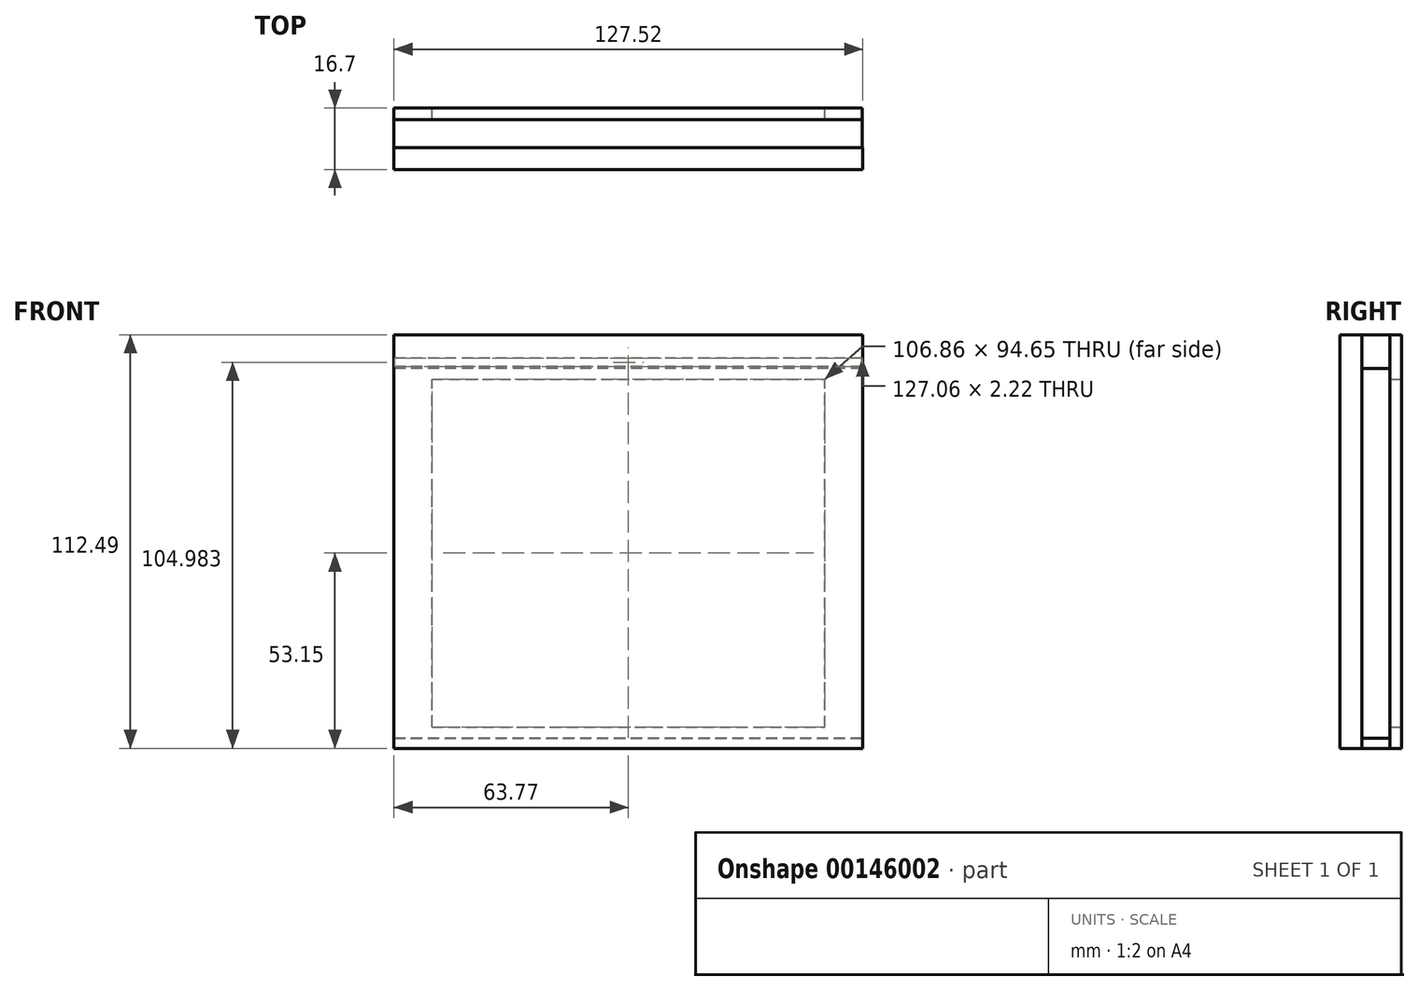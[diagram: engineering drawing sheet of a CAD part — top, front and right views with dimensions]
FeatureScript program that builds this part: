
annotation { "Feature Type Name" : "Feature", "Feature Type Description" : "" }
export const myFeature = defineFeature(function(context is Context, id is Id, definition is map)
    precondition{}
    {
        {
            var Q0;
            Q0=qCreatedBy(makeId("Front.planeOp"),FACE);
            var sketch = newSketch(context, id + "F0", { "sketchPlane" : qUnion([Q0])});
            skLineSegment(sketch, "E0.bottom", {"start": v(63.53, -52.94) * mm, "end": v(-63.53, -52.94) * mm});
            skLineSegment(sketch, "E0.top", {"start": v(63.53, 52.94) * mm, "end": v(-63.53, 52.94) * mm});
            skLineSegment(sketch, "E0.left", {"start": v(63.53, -52.94) * mm, "end": v(63.53, 52.94) * mm});
            skLineSegment(sketch, "E0.right", {"start": v(-63.53, -52.94) * mm, "end": v(-63.53, 52.94) * mm});
            skPoint(sketch, "E0.middle", {"position": v(0, 0) * mm});
            skSolve(sketch);
        }
        {
            var Q0;
            Q0=qSketchRegion(id+"F0",true);
            extrude(context, id + "F1", {"entities" : qUnion([Q0]), "depth" : 10.16 * mm});
        }
        {
            var Q0;
            Q0=qCreatedBy(makeId("Front.planeOp"),FACE);
            var sketch = newSketch(context, id + "F2", { "sketchPlane" : qUnion([Q0])});
            skLineSegment(sketch, "E1.bottom", {"start": v(-54.5, 52.94) * mm, "end": v(54.5, 52.94) * mm});
            skLineSegment(sketch, "E1.top", {"start": v(-54.5, -52.94) * mm, "end": v(54.5, -52.94) * mm});
            skLineSegment(sketch, "E1.left", {"start": v(-54.5, 52.94) * mm, "end": v(-54.5, -52.94) * mm});
            skLineSegment(sketch, "E1.right", {"start": v(54.5, 52.94) * mm, "end": v(54.5, -52.94) * mm});
            skPoint(sketch, "E1.middle", {"position": v(0, 0) * mm});
            skSolve(sketch);
        }
        {
            var Q0;
            Q0=makeQuery(id+"F2.imprint","IMPRINT",FACE,{"disambiguationData":[TD([[makeQuery(id+"F2.imprint","IMPRINT",EDGE,{"derivedFrom":sQuery(id+"F2.wireOp",EDGE,"E1.bottom")}),-1.0]])]});
            extrude(context, id + "F3", {"entities" : qUnion([Q0]), "operationType" : NewBodyOperationType.REMOVE, "depth" : 3.8 * mm});
        }
        {
            var Q0;
            Q0=qCreatedBy(makeId("Top.planeOp"),FACE);
            var sketch = newSketch(context, id + "F4", { "sketchPlane" : qUnion([Q0])});
            skCircle(sketch, "E2", {"center": v(-59.48, -1.57) * mm, "radius": 2.91 * mm});
            skSolve(sketch);
        }
        {
            var Q0;
            Q0=qSketchRegion(id+"F4",true);
            extrude(context, id + "F5", {"entities" : qUnion([Q0]), "operationType" : NewBodyOperationType.REMOVE, "depth" : 62.1 * mm, "hasSecondDirection" : true, "secondDirectionOppositeDirection" : true, "secondDirectionDepth" : 60.44 * mm});
        }
        {
            var Q0;
            Q0=qCreatedBy(makeId("Right.planeOp"),FACE);
            var sketch = newSketch(context, id + "F6", { "sketchPlane" : qUnion([Q0])});
            skLineSegment(sketch, "E3.bottom", {"start": v(-7.77, 50.72) * mm, "end": v(-2.1, 50.72) * mm});
            skLineSegment(sketch, "E3.top", {"start": v(-7.77, -51.05) * mm, "end": v(-2.1, -51.05) * mm});
            skLineSegment(sketch, "E3.left", {"start": v(-7.77, 50.72) * mm, "end": v(-7.77, -51.05) * mm});
            skLineSegment(sketch, "E3.right", {"start": v(-2.1, 50.72) * mm, "end": v(-2.1, -51.05) * mm});
            skSolve(sketch);
        }
        {
            var Q0;
            Q0=qSketchRegion(id+"F6",true);
            extrude(context, id + "F7", {"entities" : qUnion([Q0]), "operationType" : NewBodyOperationType.REMOVE, "oppositeDirection" : true, "depth" : 87.7 * mm, "hasSecondDirection" : true, "secondDirectionOppositeDirection" : false, "secondDirectionDepth" : 90.01 * mm});
        }
        {
            var Q0;
            Q0=qCreatedBy(makeId("Right.planeOp"),FACE);
            var sketch = newSketch(context, id + "F8", { "sketchPlane" : qUnion([Q0])});
            skLineSegment(sketch, "E4.bottom", {"start": v(-3.31, 51.47) * mm, "end": v(-4.6, 51.47) * mm});
            skLineSegment(sketch, "E4.top", {"start": v(-3.31, -50.55) * mm, "end": v(-4.6, -50.55) * mm});
            skLineSegment(sketch, "E4.left", {"start": v(-3.31, 51.47) * mm, "end": v(-3.31, -50.55) * mm});
            skLineSegment(sketch, "E4.right", {"start": v(-4.6, 51.47) * mm, "end": v(-4.6, -50.55) * mm});
            skSolve(sketch);
        }
        {
            var Q0;
            Q0=qSketchRegion(id+"F8",true);
            extrude(context, id + "F9", {"entities" : qUnion([Q0]), "operationType" : NewBodyOperationType.REMOVE, "depth" : 76.04 * mm, "hasSecondDirection" : true, "secondDirectionOppositeDirection" : true, "secondDirectionDepth" : 72.7 * mm});
        }
        {
            var Q0;
            Q0=qCreatedBy(makeId("Front.planeOp"),FACE);
            var sketch = newSketch(context, id + "F10", { "sketchPlane" : qUnion([Q0])});
            skLineSegment(sketch, "E5.bottom", {"start": v(63.53, 52.94) * mm, "end": v(-63.75, 52.94) * mm});
            skLineSegment(sketch, "E5.top", {"start": v(63.53, -53.15) * mm, "end": v(-63.75, -53.15) * mm});
            skLineSegment(sketch, "E5.left", {"start": v(63.53, 52.94) * mm, "end": v(63.53, -53.15) * mm});
            skLineSegment(sketch, "E5.right", {"start": v(-63.75, 52.94) * mm, "end": v(-63.75, -53.15) * mm});
            skSolve(sketch);
        }
        {
            var Q0;
            Q0=qSketchRegion(id+"F10",true);
            extrude(context, id + "F11", {"entities" : qUnion([Q0]), "operationType" : NewBodyOperationType.ADD, "oppositeDirection" : true, "depth" : 3.17 * mm});
        }
        {
            var Q0;
            Q0=qCreatedBy(makeId("Front.planeOp"),FACE);
            var sketch = newSketch(context, id + "F12", { "sketchPlane" : qUnion([Q0])});
            skLineSegment(sketch, "E6.bottom", {"start": v(-63.76, 52.95) * mm, "end": v(63.75, 52.95) * mm});
            skLineSegment(sketch, "E6.top", {"start": v(-63.76, -53.15) * mm, "end": v(63.75, -53.15) * mm});
            skLineSegment(sketch, "E6.left", {"start": v(-63.76, 52.95) * mm, "end": v(-63.76, -53.15) * mm});
            skLineSegment(sketch, "E6.right", {"start": v(63.75, 52.95) * mm, "end": v(63.75, -53.15) * mm});
            skSolve(sketch);
        }
        {
            var Q0;
            Q0=qSketchRegion(id+"F12",true);
            extrude(context, id + "F13", {"entities" : qUnion([Q0]), "operationType" : NewBodyOperationType.ADD, "depth" : 13.53 * mm, "hasSecondDirection" : true, "secondDirectionOppositeDirection" : false, "secondDirectionDepth" : 7.62 * mm});
        }
        {
            var Q0;
            Q0=qCreatedBy(makeId("Right.planeOp"),FACE);
            var sketch = newSketch(context, id + "F14", { "sketchPlane" : qUnion([Q0])});
            skLineSegment(sketch, "E7.bottom", {"start": v(0, 51.68) * mm, "end": v(-7.6, 51.68) * mm});
            skLineSegment(sketch, "E7.top", {"start": v(0, -51.05) * mm, "end": v(-7.6, -51.05) * mm});
            skLineSegment(sketch, "E7.left", {"start": v(0, 51.68) * mm, "end": v(0, -51.05) * mm});
            skLineSegment(sketch, "E7.right", {"start": v(-7.6, 51.68) * mm, "end": v(-7.6, -51.05) * mm});
            skSolve(sketch);
        }
        {
            var Q0;
            Q0=qSketchRegion(id+"F14",true);
            extrude(context, id + "F15", {"entities" : qUnion([Q0]), "operationType" : NewBodyOperationType.REMOVE, "depth" : 76.4 * mm, "hasSecondDirection" : true, "secondDirectionOppositeDirection" : true, "secondDirectionDepth" : 73.64 * mm});
        }
        {
            var Q0;
            Q0=qCreatedBy(makeId("Right.planeOp"),FACE);
            var sketch = newSketch(context, id + "F16", { "sketchPlane" : qUnion([Q0])});
            skLineSegment(sketch, "E8.bottom", {"start": v(-7.6, 52.99) * mm, "end": v(0, 52.99) * mm});
            skLineSegment(sketch, "E8.top", {"start": v(-7.6, 50.24) * mm, "end": v(0, 50.24) * mm});
            skLineSegment(sketch, "E8.left", {"start": v(-7.6, 52.99) * mm, "end": v(-7.6, 50.24) * mm});
            skLineSegment(sketch, "E8.right", {"start": v(0, 52.99) * mm, "end": v(0, 50.24) * mm});
            skLineSegment(sketch, "E9.bottom", {"start": v(-7.61, -53.13) * mm, "end": v(0, -53.13) * mm});
            skLineSegment(sketch, "E9.top", {"start": v(-7.61, -50.42) * mm, "end": v(0, -50.42) * mm});
            skLineSegment(sketch, "E9.left", {"start": v(-7.61, -53.13) * mm, "end": v(-7.61, -50.42) * mm});
            skLineSegment(sketch, "E9.right", {"start": v(0, -53.13) * mm, "end": v(0, -50.42) * mm});
            skSolve(sketch);
        }
        {
            var Q0;
            Q0=qSketchRegion(id+"F16",true);
            extrude(context, id + "F17", {"entities" : qUnion([Q0]), "operationType" : NewBodyOperationType.ADD, "depth" : 63.54 * mm, "hasSecondDirection" : true, "secondDirectionOppositeDirection" : true, "secondDirectionDepth" : 63.77 * mm});
        }
        {
            var Q0;
            Q0=makeQuery(id+"F17.opExtrude","SWEPT_FACE",FACE,{"disambiguationData":[OSD([sQuery(id+"F16.wireOp",EDGE,"E8.bottom")])]});
            var Q1;
            Q1=makeQuery(id+"F13.opExtrude","SWEPT_FACE",FACE,{"disambiguationData":[OSD([sQuery(id+"F12.wireOp",EDGE,"E6.bottom")])]});
            var Q2;
            Q2=makeQuery(id+"F11.opExtrude","SWEPT_FACE",FACE,{"disambiguationData":[OSD([sQuery(id+"F10.wireOp",EDGE,"E5.bottom")])]});
            extrude(context, id + "F18", {"entities" : qUnion([Q0, Q1, Q2]), "operationType" : NewBodyOperationType.ADD, "depth" : 6.35 * mm});
        }
        {
            var Q0;
            Q0=makeQuery(id+"F11.opExtrude","CAP_FACE",FACE,{"disambiguationData":[OSD([sQuery(id+"F10.wireOp",EDGE,"E5.bottom"),sQuery(id+"F10.wireOp",EDGE,"E5.top"),sQuery(id+"F10.wireOp",EDGE,"E5.left"),sQuery(id+"F10.wireOp",EDGE,"E5.right")])],"isStart":false});
            var sketch = newSketch(context, id + "F19", { "sketchPlane" : qUnion([Q0])});
            skLineSegment(sketch, "E10.bottom", {"start": v(-53.43, 47.32) * mm, "end": v(53.43, 47.32) * mm});
            skLineSegment(sketch, "E10.top", {"start": v(-53.43, -47.32) * mm, "end": v(53.43, -47.32) * mm});
            skLineSegment(sketch, "E10.left", {"start": v(-53.43, 47.32) * mm, "end": v(-53.43, -47.32) * mm});
            skLineSegment(sketch, "E10.right", {"start": v(53.43, 47.32) * mm, "end": v(53.43, -47.32) * mm});
            skPoint(sketch, "E10.middle", {"position": v(0, 0) * mm});
            skSolve(sketch);
        }
        {
            var Q0;
            Q0 = qSketchRegion(id + "F19", true);
            extrude(context, id + "F20", {"entities" : qUnion([Q0]), "operationType" : NewBodyOperationType.REMOVE, "oppositeDirection" : true, "depth" : 5.08 * mm});
        }
    });
